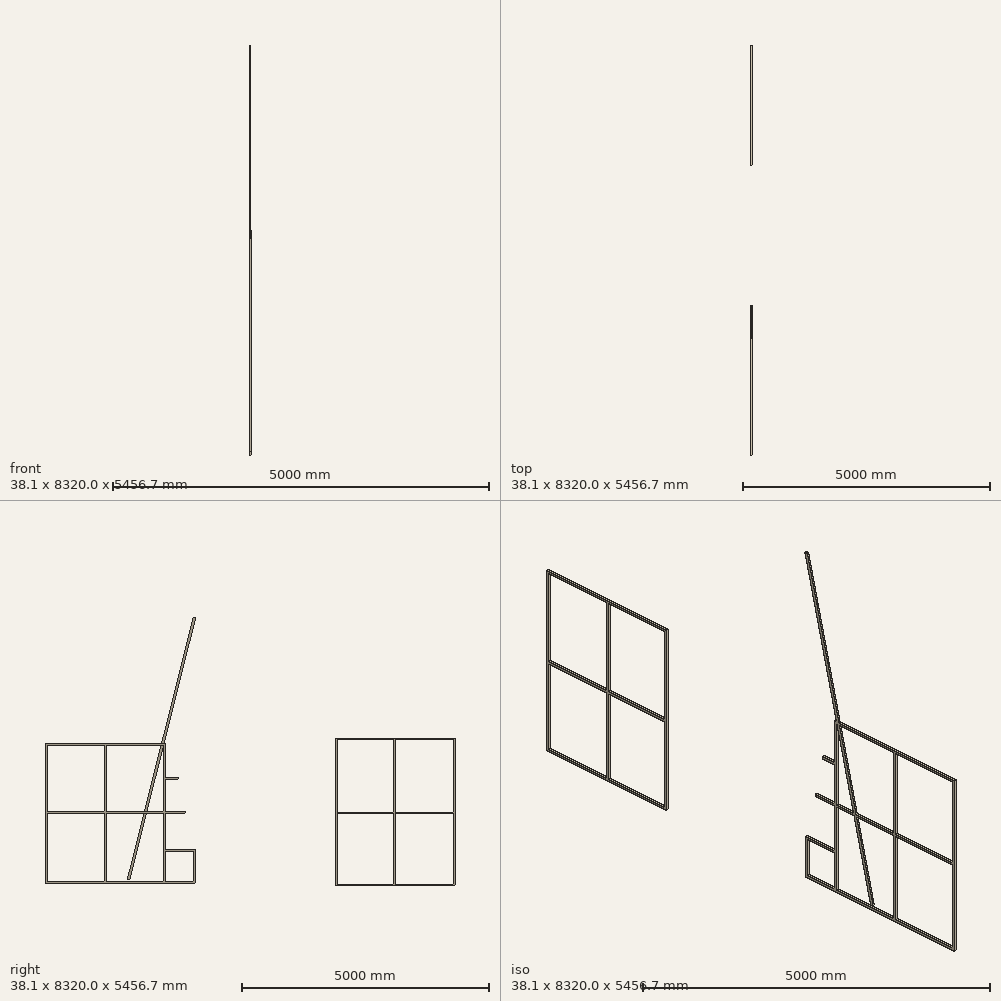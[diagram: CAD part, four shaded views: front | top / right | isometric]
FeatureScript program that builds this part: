
annotation { "Feature Type Name" : "Feature", "Feature Type Description" : "" }
export const myFeature = defineFeature(function(context is Context, id is Id, definition is map)
    precondition{}
    {
        {
            var Q0;
            Q0=qCreatedBy(makeId("Right.planeOp"),FACE);
            var sketch = newSketch(context, id + "F0", { "sketchPlane" : qUnion([Q0])});
            skLineSegment(sketch, "E0.bottom", {"start": v(-34.24, 2411.32) * mm, "end": v(3.86, 2411.32) * mm});
            skLineSegment(sketch, "E0.top", {"start": v(-34.24, -428.68) * mm, "end": v(3.86, -428.68) * mm});
            skLineSegment(sketch, "E0.left", {"start": v(-34.24, 2411.32) * mm, "end": v(-34.24, -428.68) * mm});
            skLineSegment(sketch, "E0.right", {"start": v(3.86, 2411.32) * mm, "end": v(3.86, -428.68) * mm});
            skSolve(sketch);
        }
        {
            var Q0;
            Q0 = qSketchRegion(id + "F0", true);
            extrude(context, id + "F1", {"entities" : qUnion([Q0]), "depth" : 38.1 * mm, "offsetDistance" : 25.4 * mm});
        }
        {
            var Q0;
            Q0=makeQuery(id+"F1.opExtrude","CAP_FACE",FACE,{"disambiguationData":[OSD([sQuery(id+"F0.wireOp",EDGE,"E0.bottom"),sQuery(id+"F0.wireOp",EDGE,"E0.top"),sQuery(id+"F0.wireOp",EDGE,"E0.left"),sQuery(id+"F0.wireOp",EDGE,"E0.right")])],"isStart":false});
            var sketch = newSketch(context, id + "F2", { "sketchPlane" : qUnion([Q0])});
            skLineSegment(sketch, "E1.bottom", {"start": v(3.86, 2411.32) * mm, "end": v(-2436.14, 2411.32) * mm});
            skLineSegment(sketch, "E1.top", {"start": v(3.86, 2373.22) * mm, "end": v(-2436.14, 2373.22) * mm});
            skLineSegment(sketch, "E1.left", {"start": v(3.86, 2411.32) * mm, "end": v(3.86, 2373.22) * mm});
            skLineSegment(sketch, "E1.right", {"start": v(-2436.14, 2411.32) * mm, "end": v(-2436.14, 2373.22) * mm});
            skLineSegment(sketch, "E2.bottom", {"start": v(3.86, -428.68) * mm, "end": v(-2436.14, -428.68) * mm});
            skLineSegment(sketch, "E2.top", {"start": v(3.86, -390.58) * mm, "end": v(-2436.14, -390.58) * mm});
            skLineSegment(sketch, "E2.left", {"start": v(3.86, -428.68) * mm, "end": v(3.86, -390.58) * mm});
            skLineSegment(sketch, "E2.right", {"start": v(-2436.14, -428.68) * mm, "end": v(-2436.14, -390.58) * mm});
            skLineSegment(sketch, "E3.bottom", {"start": v(3.86, 991.32) * mm, "end": v(-2436.14, 991.32) * mm});
            skLineSegment(sketch, "E3.top", {"start": v(3.86, 1029.42) * mm, "end": v(-2436.14, 1029.42) * mm});
            skLineSegment(sketch, "E3.left", {"start": v(3.86, 991.32) * mm, "end": v(3.86, 1029.42) * mm});
            skLineSegment(sketch, "E3.right", {"start": v(-2436.14, 991.32) * mm, "end": v(-2436.14, 1029.42) * mm});
            skSolve(sketch);
        }
        {
            var Q0;
            Q0 = qSketchRegion(id + "F2", true);
            extrude(context, id + "F3", {"entities" : qUnion([Q0]), "operationType" : NewBodyOperationType.ADD, "oppositeDirection" : true, "depth" : 38.1 * mm, "offsetDistance" : 25.4 * mm});
        }
        {
            var Q0;
            Q0=makeQuery(id+"F1.opExtrude","SWEPT_FACE",FACE,{"disambiguationData":[OSD([sQuery(id+"F0.wireOp",EDGE,"E0.right")])]});
            var sketch = newSketch(context, id + "F4", { "sketchPlane" : qUnion([Q0])});
            skLineSegment(sketch, "E4.bottom", {"start": v(-38.1, -428.68) * mm, "end": v(0, -428.68) * mm});
            skLineSegment(sketch, "E4.top", {"start": v(-38.1, -390.58) * mm, "end": v(0, -390.58) * mm});
            skLineSegment(sketch, "E4.left", {"start": v(-38.1, -428.68) * mm, "end": v(-38.1, -390.58) * mm});
            skLineSegment(sketch, "E4.right", {"start": v(0, -428.68) * mm, "end": v(0, -390.58) * mm});
            skLineSegment(sketch, "E5.bottom", {"start": v(-38.1, 247.52) * mm, "end": v(0, 247.52) * mm});
            skLineSegment(sketch, "E5.top", {"start": v(-38.1, 209.42) * mm, "end": v(0, 209.42) * mm});
            skLineSegment(sketch, "E5.left", {"start": v(-38.1, 247.52) * mm, "end": v(-38.1, 209.42) * mm});
            skLineSegment(sketch, "E5.right", {"start": v(0, 247.52) * mm, "end": v(0, 209.42) * mm});
            skSolve(sketch);
        }
        {
            var Q0;
            Q0 = qSketchRegion(id + "F4", true);
            extrude(context, id + "F5", {"entities" : qUnion([Q0]), "operationType" : NewBodyOperationType.ADD, "depth" : 600 * mm, "offsetDistance" : 25.4 * mm});
        }
        {
            var Q0;
            Q0=makeQuery(id+"F1.opExtrude","SWEPT_FACE",FACE,{"disambiguationData":[OSD([sQuery(id+"F0.wireOp",EDGE,"E0.right")])]});
            var sketch = newSketch(context, id + "F6", { "sketchPlane" : qUnion([Q0])});
            skLineSegment(sketch, "E6.bottom", {"start": v(-38.1, 991.32) * mm, "end": v(0, 991.32) * mm});
            skLineSegment(sketch, "E6.top", {"start": v(-38.1, 1029.42) * mm, "end": v(0, 1029.42) * mm});
            skLineSegment(sketch, "E6.left", {"start": v(-38.1, 991.32) * mm, "end": v(-38.1, 1029.42) * mm});
            skLineSegment(sketch, "E6.right", {"start": v(0, 991.32) * mm, "end": v(0, 1029.42) * mm});
            skSolve(sketch);
        }
        {
            var Q0;
            Q0 = qSketchRegion(id + "F6", true);
            extrude(context, id + "F7", {"entities" : qUnion([Q0]), "operationType" : NewBodyOperationType.ADD, "depth" : 400 * mm, "offsetDistance" : 25.4 * mm});
        }
        {
            var Q0;
            {var subQ12=sQuery(id+"F0.wireOp",EDGE,"E0.bottom");var subQ13=sQuery(id+"F0.wireOp",EDGE,"E0.right");Q0=makeQuery(id+"F7.boolean.opBoolean","SPLIT",FACE,{"disambiguationData":[TD([makeQuery(id+"F1.opExtrude","SWEPT_FACE",FACE,{"disambiguationData":[OSD([subQ12])]})])],"derivedFrom":makeQuery(id+"F1.opExtrude","SWEPT_FACE",FACE,{"disambiguationData":[OSD([subQ13])]})});}
            var sketch = newSketch(context, id + "F8", { "sketchPlane" : qUnion([Q0])});
            skLineSegment(sketch, "E7.bottom", {"start": v(-38.1, 1717.34) * mm, "end": v(0, 1717.34) * mm});
            skLineSegment(sketch, "E7.top", {"start": v(-38.1, 1679.24) * mm, "end": v(0, 1679.24) * mm});
            skLineSegment(sketch, "E7.left", {"start": v(-38.1, 1717.34) * mm, "end": v(-38.1, 1679.24) * mm});
            skLineSegment(sketch, "E7.right", {"start": v(0, 1717.34) * mm, "end": v(0, 1679.24) * mm});
            skSolve(sketch);
        }
        {
            var Q0;
            Q0 = qSketchRegion(id + "F8", true);
            extrude(context, id + "F9", {"entities" : qUnion([Q0]), "operationType" : NewBodyOperationType.ADD, "depth" : 250 * mm, "offsetDistance" : 25.4 * mm});
        }
        {
            var Q0;
            Q0=makeQuery(id+"F5.opExtrude","SWEPT_FACE",FACE,{"disambiguationData":[OSD([sQuery(id+"F4.wireOp",EDGE,"E5.top")])]});
            var sketch = newSketch(context, id + "F10", { "sketchPlane" : qUnion([Q0])});
            skLineSegment(sketch, "E8.bottom", {"start": v(38.1, -603.86) * mm, "end": v(0, -603.86) * mm});
            skLineSegment(sketch, "E8.top", {"start": v(38.1, -565.76) * mm, "end": v(0, -565.76) * mm});
            skLineSegment(sketch, "E8.left", {"start": v(38.1, -603.86) * mm, "end": v(38.1, -565.76) * mm});
            skLineSegment(sketch, "E8.right", {"start": v(0, -603.86) * mm, "end": v(0, -565.76) * mm});
            skSolve(sketch);
        }
        {
            var Q0;
            Q0 = qSketchRegion(id + "F10", true);
            var Q1;
            Q1=makeQuery(id+"F5.opExtrude","SWEPT_FACE",FACE,{"disambiguationData":[OSD([sQuery(id+"F4.wireOp",EDGE,"E4.top")])]});
            extrude(context, id + "F11", {"entities" : qUnion([Q0]), "operationType" : NewBodyOperationType.ADD, "endBound" : BoundingType.UP_TO_SURFACE, "depth" : 25.4 * mm, "endBoundEntityFace" : qUnion([Q1]), "offsetDistance" : 25.4 * mm});
        }
        {
            var Q0;
            Q0=makeQuery(id+"F3.opExtrude","SWEPT_FACE",FACE,{"disambiguationData":[OSD([sQuery(id+"F2.wireOp",EDGE,"E1.top")])]});
            var sketch = newSketch(context, id + "F12", { "sketchPlane" : qUnion([Q0])});
            skLineSegment(sketch, "E9.bottom", {"start": v(0, 1235.19) * mm, "end": v(38.1, 1235.19) * mm});
            skLineSegment(sketch, "E9.top", {"start": v(0, 1197.09) * mm, "end": v(38.1, 1197.09) * mm});
            skLineSegment(sketch, "E9.left", {"start": v(0, 1235.19) * mm, "end": v(0, 1197.09) * mm});
            skLineSegment(sketch, "E9.right", {"start": v(38.1, 1235.19) * mm, "end": v(38.1, 1197.09) * mm});
            skSolve(sketch);
        }
        {
            var Q0;
            Q0 = qSketchRegion(id + "F12", true);
            var Q1;
            Q1=makeQuery(id+"F3.opExtrude","SWEPT_FACE",FACE,{"disambiguationData":[OSD([sQuery(id+"F2.wireOp",EDGE,"E2.top")])]});
            extrude(context, id + "F13", {"entities" : qUnion([Q0]), "operationType" : NewBodyOperationType.ADD, "endBound" : BoundingType.UP_TO_SURFACE, "depth" : 25.4 * mm, "endBoundEntityFace" : qUnion([Q1]), "offsetDistance" : 25.4 * mm});
        }
        {
            var Q0;
            {var subQ8=sQuery(id+"F2.wireOp",EDGE,"E1.right");var subQ14=sQuery(id+"F2.wireOp",EDGE,"E1.top");Q0=makeQuery(id+"F13.boolean.opBoolean","SPLIT",FACE,{"disambiguationData":[TD([makeQuery(id+"F3.opExtrude","SWEPT_FACE",FACE,{"disambiguationData":[OSD([subQ8])]})])],"derivedFrom":makeQuery(id+"F3.opExtrude","SWEPT_FACE",FACE,{"disambiguationData":[OSD([subQ14])]})});}
            var sketch = newSketch(context, id + "F14", { "sketchPlane" : qUnion([Q0])});
            skLineSegment(sketch, "E10.bottom", {"start": v(38.1, 2436.14) * mm, "end": v(0, 2436.14) * mm});
            skLineSegment(sketch, "E10.top", {"start": v(38.1, 2398.04) * mm, "end": v(0, 2398.04) * mm});
            skLineSegment(sketch, "E10.left", {"start": v(38.1, 2436.14) * mm, "end": v(38.1, 2398.04) * mm});
            skLineSegment(sketch, "E10.right", {"start": v(0, 2436.14) * mm, "end": v(0, 2398.04) * mm});
            skSolve(sketch);
        }
        {
            var Q0;
            Q0 = qSketchRegion(id + "F14", true);
            var Q1;
            {var subQ4=sQuery(id+"F2.wireOp",EDGE,"E2.right");var subQ6=sQuery(id+"F2.wireOp",EDGE,"E2.top");Q1=makeQuery(id+"F13.boolean.opBoolean","SPLIT",FACE,{"disambiguationData":[TD([makeQuery(id+"F3.opExtrude","SWEPT_FACE",FACE,{"disambiguationData":[OSD([subQ4])]})])],"derivedFrom":makeQuery(id+"F3.opExtrude","SWEPT_FACE",FACE,{"disambiguationData":[OSD([subQ6])]})});}
            extrude(context, id + "F15", {"entities" : qUnion([Q0]), "operationType" : NewBodyOperationType.ADD, "endBound" : BoundingType.UP_TO_SURFACE, "depth" : 25.4 * mm, "endBoundEntityFace" : qUnion([Q1]), "offsetDistance" : 25.4 * mm});
        }
        {
            var Q0;
            Q0=qCreatedBy(makeId("Right.planeOp"),FACE);
            var sketch = newSketch(context, id + "F16", { "sketchPlane" : qUnion([Q0])});
            skLineSegment(sketch, "E11", {"start": v(-725.31, -362.46) * mm, "end": v(605.36, 4921.77) * mm});
            skLineSegment(sketch, "E12", {"start": v(605.36, 4921.77) * mm, "end": v(617.76, 4971.03) * mm});
            skLineSegment(sketch, "E13", {"start": v(617.76, 4971.03) * mm, "end": v(-725.31, -362.46) * mm});
            skLineSegment(sketch, "E14", {"start": v(-725.31, -362.46) * mm, "end": v(-774.58, -350.06) * mm});
            skLineSegment(sketch, "E15", {"start": v(-774.58, -350.06) * mm, "end": v(566.2, 4974.27) * mm});
            skLineSegment(sketch, "E16", {"start": v(566.2, 4974.27) * mm, "end": v(617.76, 4971.03) * mm});
            skSolve(sketch);
        }
        {
            var Q0;
            Q0 = qSketchRegion(id + "F16", true);
            extrude(context, id + "F17", {"entities" : qUnion([Q0]), "operationType" : NewBodyOperationType.ADD, "depth" : 25.4 * mm, "offsetDistance" : 25.4 * mm});
        }
        {
            var Q0;
            Q0 = qSketchRegion(id + "F16", true);
            extrude(context, id + "F18", {"entities" : qUnion([Q0]), "operationType" : NewBodyOperationType.ADD, "depth" : 25.4 * mm, "offsetDistance" : 25.4 * mm});
        }
        {
            var Q0;
            Q0=qCreatedBy(makeId("Right.planeOp"),FACE);
            var sketch = newSketch(context, id + "F19", { "sketchPlane" : qUnion([Q0])});
            skLineSegment(sketch, "E17.bottom", {"start": v(3443.86, 2517.55) * mm, "end": v(5883.86, 2517.55) * mm});
            skLineSegment(sketch, "E17.top", {"start": v(3443.86, -482.45) * mm, "end": v(5883.86, -482.45) * mm});
            skLineSegment(sketch, "E17.left", {"start": v(3443.86, 2517.55) * mm, "end": v(3443.86, -482.45) * mm});
            skLineSegment(sketch, "E17.right", {"start": v(5883.86, 2517.55) * mm, "end": v(5883.86, -482.45) * mm});
            skLineSegment(sketch, "E18.bottom", {"start": v(3481.96, 2479.45) * mm, "end": v(5845.76, 2479.45) * mm});
            skLineSegment(sketch, "E18.top", {"start": v(3481.96, -444.35) * mm, "end": v(5845.76, -444.35) * mm});
            skLineSegment(sketch, "E18.left", {"start": v(3481.96, 2479.45) * mm, "end": v(3481.96, -444.35) * mm});
            skLineSegment(sketch, "E18.right", {"start": v(5845.76, 2479.45) * mm, "end": v(5845.76, -444.35) * mm});
            skSolve(sketch);
        }
        {
            var Q0;
            Q0 = qSketchRegion(id + "F19", true);
            extrude(context, id + "F20", {"entities" : qUnion([Q0]), "depth" : 38.1 * mm, "offsetDistance" : 25.4 * mm});
        }
        {
            var Q0;
            Q0=makeQuery(id+"F20.opExtrude","CAP_FACE",FACE,{"disambiguationData":[OSD([sQuery(id+"F19.wireOp",EDGE,"E17.bottom"),sQuery(id+"F19.wireOp",EDGE,"E17.top"),sQuery(id+"F19.wireOp",EDGE,"E17.left"),sQuery(id+"F19.wireOp",EDGE,"E17.right"),sQuery(id+"F19.wireOp",EDGE,"E18.bottom"),sQuery(id+"F19.wireOp",EDGE,"E18.top"),sQuery(id+"F19.wireOp",EDGE,"E18.left"),sQuery(id+"F19.wireOp",EDGE,"E18.right")])],"isStart":false});
            var sketch = newSketch(context, id + "F21", { "sketchPlane" : qUnion([Q0])});
            skLineSegment(sketch, "E19.bottom", {"start": v(4625.76, 2517.55) * mm, "end": v(4663.86, 2517.55) * mm});
            skLineSegment(sketch, "E19.top", {"start": v(4625.76, -482.45) * mm, "end": v(4663.86, -482.45) * mm});
            skLineSegment(sketch, "E19.left", {"start": v(4625.76, 2517.55) * mm, "end": v(4625.76, -482.45) * mm});
            skLineSegment(sketch, "E19.right", {"start": v(4663.86, 2517.55) * mm, "end": v(4663.86, -482.45) * mm});
            skSolve(sketch);
        }
        {
            var Q0;
            Q0 = qSketchRegion(id + "F21", true);
            extrude(context, id + "F22", {"entities" : qUnion([Q0]), "operationType" : NewBodyOperationType.ADD, "oppositeDirection" : true, "depth" : 38.1 * mm, "offsetDistance" : 25.4 * mm});
        }
        {
            var Q0;
            Q0=makeQuery(id+"F22.boolean.opBoolean","MERGE",FACE,{"derivedFrom":[makeQuery(id+"F20.opExtrude","CAP_FACE",FACE,{"disambiguationData":[OSD([sQuery(id+"F19.wireOp",EDGE,"E17.bottom"),sQuery(id+"F19.wireOp",EDGE,"E17.top"),sQuery(id+"F19.wireOp",EDGE,"E17.left"),sQuery(id+"F19.wireOp",EDGE,"E17.right"),sQuery(id+"F19.wireOp",EDGE,"E18.bottom"),sQuery(id+"F19.wireOp",EDGE,"E18.top"),sQuery(id+"F19.wireOp",EDGE,"E18.left"),sQuery(id+"F19.wireOp",EDGE,"E18.right")])],"isStart":false}),makeQuery(id+"F22.opExtrude","CAP_FACE",FACE,{"disambiguationData":[OSD([sQuery(id+"F21.wireOp",EDGE,"E19.bottom"),sQuery(id+"F21.wireOp",EDGE,"E19.top"),sQuery(id+"F21.wireOp",EDGE,"E19.left"),sQuery(id+"F21.wireOp",EDGE,"E19.right")])],"isStart":true})]});
            var sketch = newSketch(context, id + "F23", { "sketchPlane" : qUnion([Q0])});
            skLineSegment(sketch, "E20.bottom", {"start": v(3443.86, 979.45) * mm, "end": v(5883.86, 979.45) * mm});
            skLineSegment(sketch, "E20.top", {"start": v(3443.86, 1017.55) * mm, "end": v(5883.86, 1017.55) * mm});
            skLineSegment(sketch, "E20.left", {"start": v(3443.86, 979.45) * mm, "end": v(3443.86, 1017.55) * mm});
            skLineSegment(sketch, "E20.right", {"start": v(5883.86, 979.45) * mm, "end": v(5883.86, 1017.55) * mm});
            skSolve(sketch);
        }
        {
            var Q0;
            Q0 = qSketchRegion(id + "F23", true);
            extrude(context, id + "F24", {"entities" : qUnion([Q0]), "operationType" : NewBodyOperationType.ADD, "oppositeDirection" : true, "depth" : 38.1 * mm, "offsetDistance" : 25.4 * mm});
        }
    });
